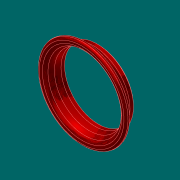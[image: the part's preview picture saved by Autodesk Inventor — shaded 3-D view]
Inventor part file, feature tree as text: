
AUTODESK INVENTOR PART (.ipt)
format: ipt  version: 2017.3 (Build 213257000, 257)  size: 292,864 bytes
history: native  units: in
note: dims shown in document units (in); Inventor stores cm internally (conversion verified against a paired STEP export)
features: sketch x4, extrude x3, fillet x2, revolve x1, chamfer x1, projected_geometry x1
ambient origin geometry x8: Origin, YZ Plane, XZ Plane, XY Plane, X Axis, Y Axis, Z Axis, Center Point
bodies: Solid1 (feature_tree)
feature tree (12):
  revolve  "Revolution1"  [1 undecoded]
  extrude  "Extrusion8"  Depth=9.5in
  fillet  "Fillet14"  [1 undecoded]
  extrude  "Extrusion10"  Depth=5.7in
  extrude  "Extrusion9"  Depth=0.751in
  fillet  "Fillet15"  Radius=2.052in
  chamfer  "Chamfer4"  Distance=0.265in
  sketch  "Sketch1"  dims[d1=30.75in d3=28.5in]
  sketch  "Sketch9"  dims[d4=28.5in d5=9.5in d6=15.0deg]
  sketch  "Sketch10"  dims[d7=5.7in d8=0.1412in]
  sketch  "Sketch11"  dims[d9=3.42in d10=0.1935in d11=2.052in d12=0.265in d13=1.2312in d14=0.3631in d17=0.7387in d18=0.5497in d19=3.0in d20=90.0deg d37=0.0in d94=37.8796in d95=30.516in d96=1.375in d97=0.0in d98=0.0312in d99=6.3386in d100=0.751in d101=35.2368in d103=0.5in d104=0.0in d105=0.0312in d106=0.0312in d107=0.125in d108=45.0deg d109=0.25in d110=0.0in d111=0.49in d112=0.751in]
  projected_geometry  "Projected Loop1"
note: 2 required parameter values undecoded (feature->parameter linkage not recoverable at this tier; creation-order binding heuristic only, values carry confidence <= 0.55)